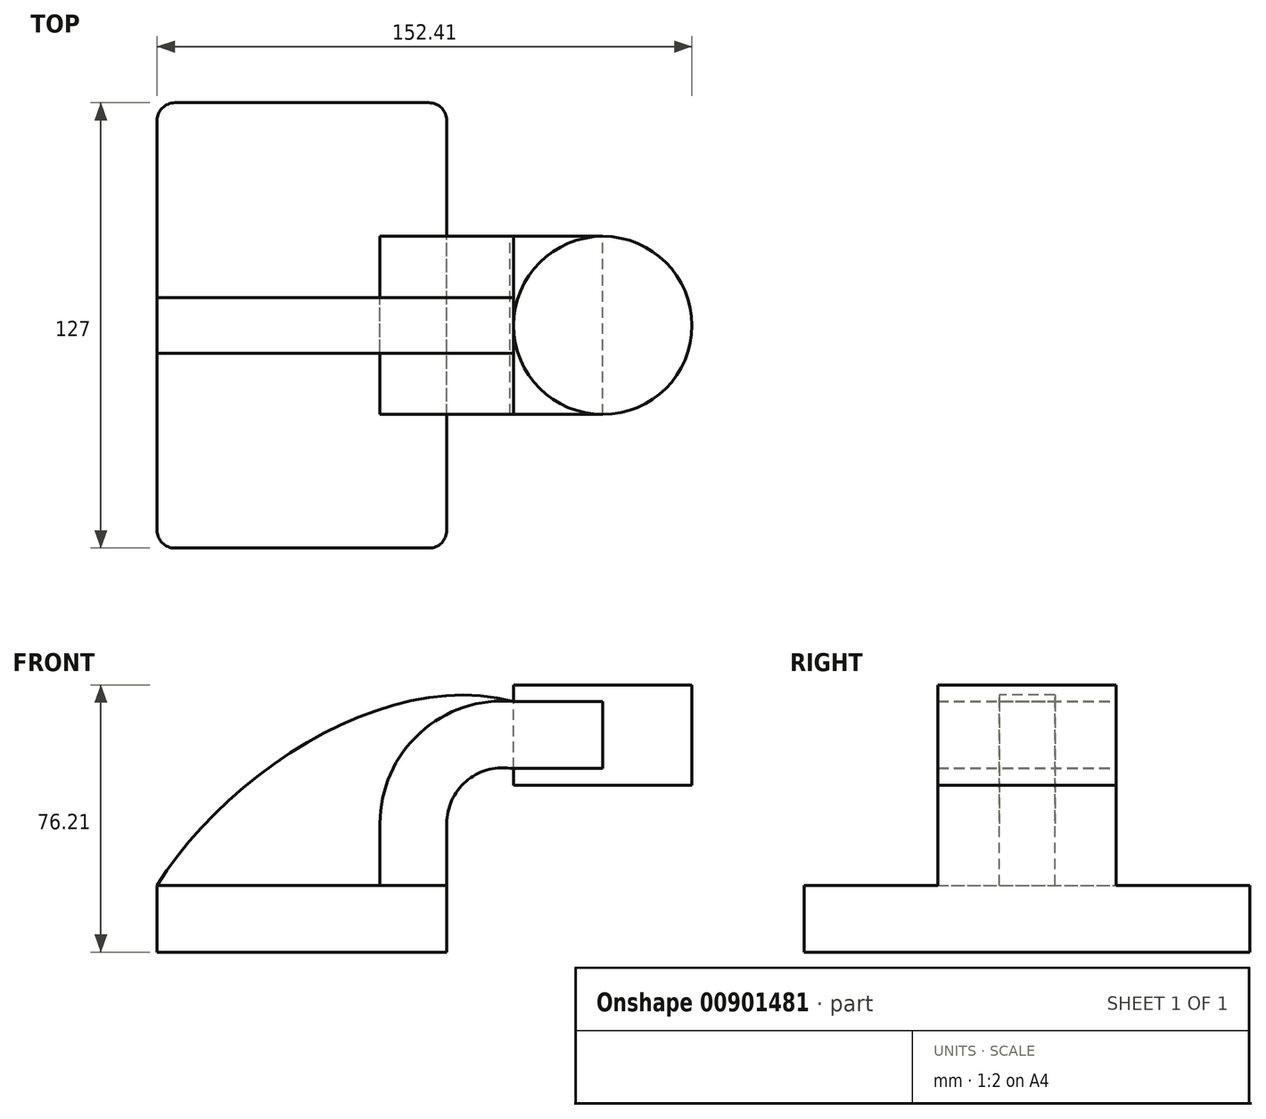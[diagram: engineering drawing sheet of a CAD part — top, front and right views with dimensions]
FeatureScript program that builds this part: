
annotation { "Feature Type Name" : "Feature", "Feature Type Description" : "" }
export const myFeature = defineFeature(function(context is Context, id is Id, definition is map)
    precondition{}
    {
        {
            var Q0;
            Q0=qCreatedBy(makeId("Front.planeOp"),FACE);
            var sketch = newSketch(context, id + "F0", { "sketchPlane" : qUnion([Q0])});
            skLineSegment(sketch, "E0.bottom", {"start": v(41.27, 9.53) * mm, "end": v(-41.28, 9.53) * mm});
            skLineSegment(sketch, "E0.top", {"start": v(41.28, -9.52) * mm, "end": v(-41.27, -9.52) * mm});
            skLineSegment(sketch, "E0.left", {"start": v(41.28, 9.53) * mm, "end": v(41.28, -9.52) * mm});
            skLineSegment(sketch, "E0.right", {"start": v(-41.28, 9.53) * mm, "end": v(-41.27, -9.52) * mm});
            skPoint(sketch, "E0.middle", {"position": v(0, 0) * mm});
            skLineSegment(sketch, "E1", {"start": v(41.27, 9.53) * mm, "end": v(41.27, 27.15) * mm});
            skLineSegment(sketch, "E2.bottom", {"start": v(60.33, 38.1) * mm, "end": v(111.13, 38.1) * mm});
            skLineSegment(sketch, "E2.top", {"start": v(60.33, 66.68) * mm, "end": v(111.13, 66.68) * mm});
            skLineSegment(sketch, "E2.left", {"start": v(60.33, 38.1) * mm, "end": v(60.33, 66.68) * mm});
            skLineSegment(sketch, "E2.right", {"start": v(111.13, 38.1) * mm, "end": v(111.13, 66.68) * mm});
            skPoint(sketch, "E2.middle", {"position": v(85.73, 52.39) * mm});
            skArc(sketch, "E3", {"start": v(41.27, 27.15) * mm, "mid": v(46.71, 39.11) * mm, "end": v(59.3, 42.88) * mm});
            skLineSegment(sketch, "E4", {"start": v(59.3, 42.88) * mm, "end": v(85.72, 42.88) * mm});
            skLineSegment(sketch, "E5.0", {"start": v(60.35, 61.93) * mm, "end": v(85.72, 61.93) * mm});
            skArc(sketch, "E5.1", {"start": v(22.22, 27.15) * mm, "mid": v(33.61, 52.95) * mm, "end": v(60.35, 61.93) * mm});
            skLineSegment(sketch, "E5.2", {"start": v(22.22, 9.53) * mm, "end": v(22.22, 27.15) * mm});
            skLineSegment(sketch, "E6", {"start": v(85.72, 61.93) * mm, "end": v(85.72, 42.88) * mm});
            skFitSpline(sketch, "E7", {"points": [v(-41.28, 9.52) * mm, v(60.35, 61.93) * mm], "startDerivative": vector(60.83, 97.38) * mm, "endDerivative": vector(106.37, -29.23) * mm});
            skLineSegment(sketch, "E8", {"start": v(85.73, 66.68) * mm, "end": v(85.73, 38.1) * mm});
            skSolve(sketch);
        }
        {
            var Q0;
            Q0=makeQuery(id+"F0.imprint","IMPRINT",FACE,{"disambiguationData":[TD([[makeQuery(id+"F0.imprint","IMPRINT",EDGE,{"derivedFrom":sQuery(id+"F0.wireOp",EDGE,"E0.top")}),-1.0]])]});
            extrude(context, id + "F1", {"entities" : qUnion([Q0]), "endBound" : BoundingType.SYMMETRIC, "depth" : 127 * mm, "offsetDistance" : 25.4 * mm});
        }
        {
            var Q0;
            {var subQ6=sQuery(id+"F0.wireOp",EDGE,"E1");Q0=makeQuery(id+"F0.imprint","IMPRINT",FACE,{"disambiguationData":[TD([[makeQuery(id+"F0.imprint","IMPRINT",EDGE,{"derivedFrom":subQ6}),1.0]])]});}
            var Q1;
            {var subQ1=sQuery(id+"F0.wireOp",EDGE,"E5.0");Q1=makeQuery(id+"F0.imprint","IMPRINT",FACE,{"disambiguationData":[TD([[makeQuery(id+"F0.imprint","IMPRINT",EDGE,{"derivedFrom":subQ1}),-1.0]])]});}
            extrude(context, id + "F2", {"entities" : qUnion([Q0, Q1]), "operationType" : NewBodyOperationType.ADD, "endBound" : BoundingType.SYMMETRIC, "depth" : 50.8 * mm, "offsetDistance" : 25.4 * mm});
        }
        {
            var Q0;
            {var subQ0=sQuery(id+"F0.wireOp",EDGE,"E5.2");Q0=makeQuery(id+"F0.imprint","IMPRINT",FACE,{"disambiguationData":[TD([[makeQuery(id+"F0.imprint","IMPRINT",EDGE,{"derivedFrom":subQ0}),1.0]])]});}
            extrude(context, id + "F3", {"entities" : qUnion([Q0]), "endBound" : BoundingType.SYMMETRIC, "depth" : 15.88 * mm, "offsetDistance" : 25.4 * mm});
        }
        {
            var Q0;
            {var subQ4=sQuery(id+"F0.wireOp",EDGE,"E2.right");Q0=makeQuery(id+"F0.imprint","IMPRINT",FACE,{"disambiguationData":[TD([[makeQuery(id+"F0.imprint","IMPRINT",EDGE,{"derivedFrom":subQ4}),1.0]])]});}
            var Q1;
            Q1=sQuery(id+"F0.wireOp",EDGE,"E8");
            revolve(context, id + "F4", {"surfaceOperationType" : NewSurfaceOperationType.NEW, "entities" : qUnion([Q0]), "axis" : qUnion([Q1]), "revolveType" : RevolveType.FULL});
        }
        {
            var Q0;
            Q0=makeQuery(id+"F1.opExtrude","CAP_EDGE",EDGE,{"disambiguationData":[OSD([sQuery(id+"F0.wireOp",EDGE,"E0.left")])],"isStart":true});
            var Q1;
            Q1=makeQuery(id+"F1.opExtrude","CAP_EDGE",EDGE,{"disambiguationData":[OSD([sQuery(id+"F0.wireOp",EDGE,"E0.right")])],"isStart":true});
            var Q2;
            Q2=makeQuery(id+"F1.opExtrude","CAP_EDGE",EDGE,{"disambiguationData":[OSD([sQuery(id+"F0.wireOp",EDGE,"E0.right")])],"isStart":false});
            var Q3;
            Q3=makeQuery(id+"F1.opExtrude","CAP_EDGE",EDGE,{"disambiguationData":[OSD([sQuery(id+"F0.wireOp",EDGE,"E0.left")])],"isStart":false});
            fillet(context, id + "F5", {"entities" : qUnion([Q0, Q1, Q2, Q3]), "radius" : 5.08 * mm, "tangentPropagation" : true, "allowEdgeOverflow" : false});
        }
    });
